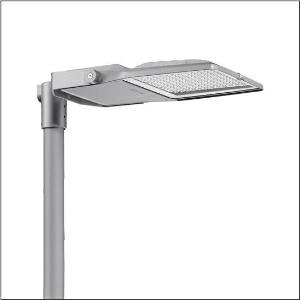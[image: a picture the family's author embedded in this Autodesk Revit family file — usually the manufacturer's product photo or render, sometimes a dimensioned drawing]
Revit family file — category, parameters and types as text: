
# Revit family: floodlight_fl_21_midi___pl33t_5xa7785e2f3a_9b27
name_source: partatom
category: Lighting Fixtures
units: mm (PartAtom-declared; Revit-internal decimal feet)

## family parameters
Cut with Voids When Loaded = No
Host = Face
Light Source = No
Part Type = Normal
Room Calculation Point = No
Round Connector Dimension = Use Diameter
Shared = No

## types (1)
- --- (1 x LED, 26630 lm, 212.4 W, 3000K)
    Apparent Load = 212 VA
    CIE Flux Codes = 26 75 99 100 100
    Color Rendering = 70
    Color Temperature = 3000K
    Default Elevation = 1800 mm
    Description = Floodlight FL 21 midi, floodlight, primary light control with lens, of PMMA, primary optical cover: protective disc, of toughened safety glass, transparent, light distribution: PL33T, light emission: direct distribution, installation type: surface-mounted, LED, High Power LED, rated luminous flux: 26.630lm, luminous efficacy: 125lm/W, light colour: 730, colour temperature: 3000K, control gear: ECG Smart Interface, control: flexible luminous flux parameterisation, time-dependent luminous flux control, constant luminous flux control, overheat protection, pre-setting: logarithmic dimming characteristic, with terminal, 6-pole, mains connection: 220..240V, AC, 50/60Hz, start of lifetime: 212W, end of service life: 231W, reduction: 95W, luminaire housing, of diecast aluminium, powder-coated, Siteco® metallic grey (DB 702S), sealing non-destructively replaceable, please order mast flange separately, mast bracket, of steel, galvanised, powder-coated, Siteco® metallic grey (DB 702S), Smart Interface above, protection rating (complete): IP66, insulation class (complete): insulation class II (safety insulation), certification: CE, ENEC, VDE, protection symbol: D, impact resistance: IK08, permissible operating ambient temperature: -20..+40°C, permissible operating ambient temperature for outdoor applications: -40..+50°C, standard: DIN EN 12944, LABS conformity tested according to VDMA 24364:2018-05, packaging unit: 1 piece

Light Distribution: PL33T
    Height = 76 mm
    Lamp = 1 x LED
    Lamp Light Flux = 26630 lm
    Lamp Power = 212.4 W
    Lamp count = 1
    Length = 657 mm
    Luminous efficacy = 125 lm/W
    Manufacturer = Siteco
    ModVariant = No
    Model = 5XA7785E2F3A
    Number of Poles = 1
    OnlyDefault = Yes
    Power Factor = 1
    Product Name = Floodlight FL 21 midi | PL33T
    Product group = floodlight | pylon annexe
    ProductGroupID = 6200
    Protection Class = Protection class II
    Protection Degree = IP 66
    RLX_Detail_Level = 1
    RLX_Emergency_Light_Flux = 0 lm
    RLX_Emergency_Type = 0
    RLX_Emergency_Type_DB = No
    RlxData = <blob elided: 153377 chars, md5=628b1c87>
    Socket = socket
    Standby Power = 0 W
    System Light Flux = 26630 lm
    System Power = 212 W
    Type Comments = factory setting: luminous flux: 100 % | dim-lin: 254 | 710 mA
    Type Image = l_1007123.jpg
    URL = http://relux.com
    VarID = @adj_120953
    Voltage = 0 V
    Weight = 0.00 kg
    Width = 442 mm

## geometry (parser evidence)
native form markers: Blend x4, Sweep x14
no freeform markers — native parametric forms only
